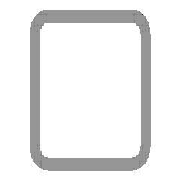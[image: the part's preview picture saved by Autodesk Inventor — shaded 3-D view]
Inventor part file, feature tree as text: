
AUTODESK INVENTOR PART (.ipt)
format: ipt  version: 2025 (Build 290162010, 162A)  size: 133,120 bytes
history: native  units: mm (DEFAULTED — no unit token found)
features: other x4, sketch x1, plane x1
ambient origin geometry x8: Origin, YZ Plane, XZ Plane, XY Plane, X Axis, Y Axis, Z Axis, Center Point
bodies: Solid1 (feature_tree), Body (feature_tree)
feature tree (6):
  parser-record x1  (decoder bookkeeping rows leaked as tree rows — omitted from the tree; the rows remain in map.json)
  other  "Driven Length"
  other  "Start Plane"
  other  "End Plane"
  sketch  "Sketch3"  dims[d3=300.0mm d4=0.0mm d7=6.0mm d9=50.0mm d11=50.0mm d12=3.0mm d13=-0.0mm d14=300.0mm d15=25.0mm d16=25.0mm d17=90.0deg d18=300.0mm]
  plane  "Work Plane3"
